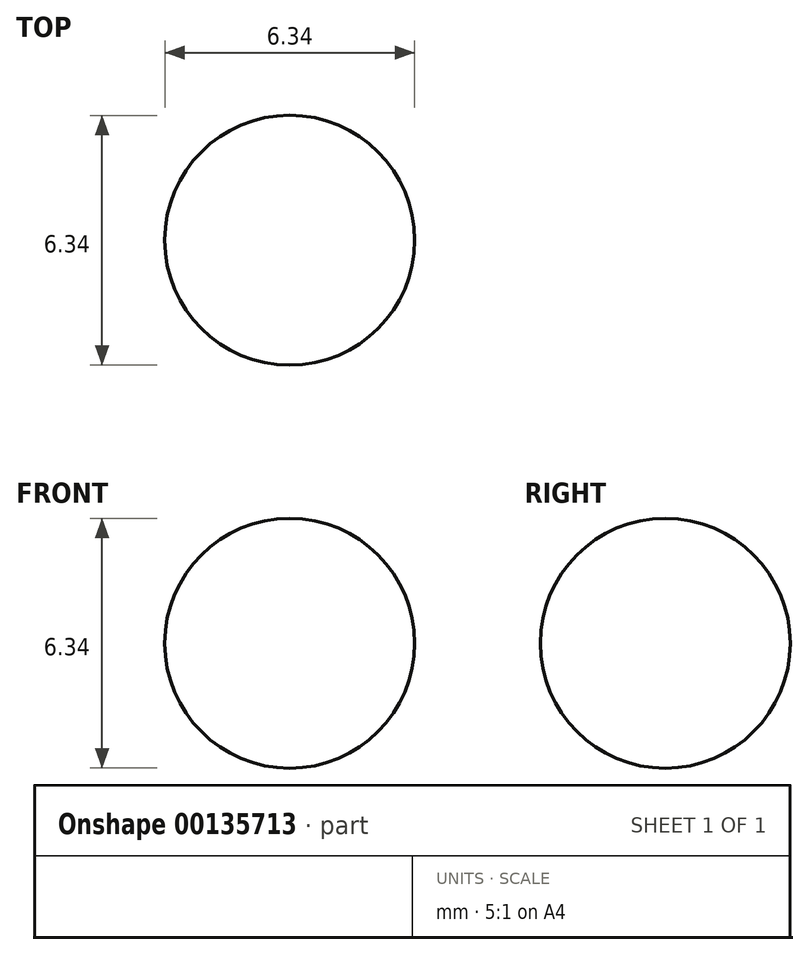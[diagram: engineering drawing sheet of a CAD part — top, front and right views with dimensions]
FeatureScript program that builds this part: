
annotation { "Feature Type Name" : "Feature", "Feature Type Description" : "" }
export const myFeature = defineFeature(function(context is Context, id is Id, definition is map)
    precondition{}
    {
        {
            var Q0;
            Q0=qCreatedBy(makeId("Front.planeOp"),FACE);
            var sketch = newSketch(context, id + "F0", { "sketchPlane" : qUnion([Q0])});
            skArc(sketch, "E0", {"start": v(0, -3.18) * mm, "mid": v(3.18, 0) * mm, "end": v(0, 3.18) * mm});
            skLineSegment(sketch, "E1", {"start": v(0, 3.18) * mm, "end": v(0, -3.18) * mm});
            skSolve(sketch);
        }
        {
            var Q0;
            Q0=makeQuery(id+"F0.imprint","IMPRINT",FACE,{"disambiguationData":[TD([[makeQuery(id+"F0.imprint","IMPRINT",EDGE,{"derivedFrom":sQuery(id+"F0.wireOp",EDGE,"E0")}),1.0]])]});
            var Q1;
            Q1=sQuery(id+"F0.wireOp",EDGE,"E1");
            revolve(context, id + "F1", {"entities" : qUnion([Q0]), "axis" : qUnion([Q1]), "revolveType" : RevolveType.FULL});
        }
    });
